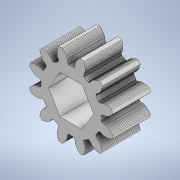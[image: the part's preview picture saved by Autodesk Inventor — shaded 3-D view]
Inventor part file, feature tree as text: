
AUTODESK INVENTOR PART (.ipt)
format: ipt  version: 2022 (Build 260153000, 153)  size: 2,677,760 bytes
history: native  units: mm
features: sketch x2, extrude x2
ambient origin geometry x8: Origin, YZ Plane, XZ Plane, XY Plane, X Axis, Y Axis, Z Axis, Center Point
bodies: Solid1 (feature_tree)
feature tree (4):
  sketch  "Sketch1"  dims[d10=6.2mm d11=0.0mm d30=3.1mm]
  extrude  "Extrusion1"  Depth=6.2mm
  extrude  "Extrusion8"  Depth=10.0mm
  sketch  "Sketch4"  dims[d31=60.0mm d33=360.0deg d37=0.5mm d38=10.0mm d39=0.0mm]
